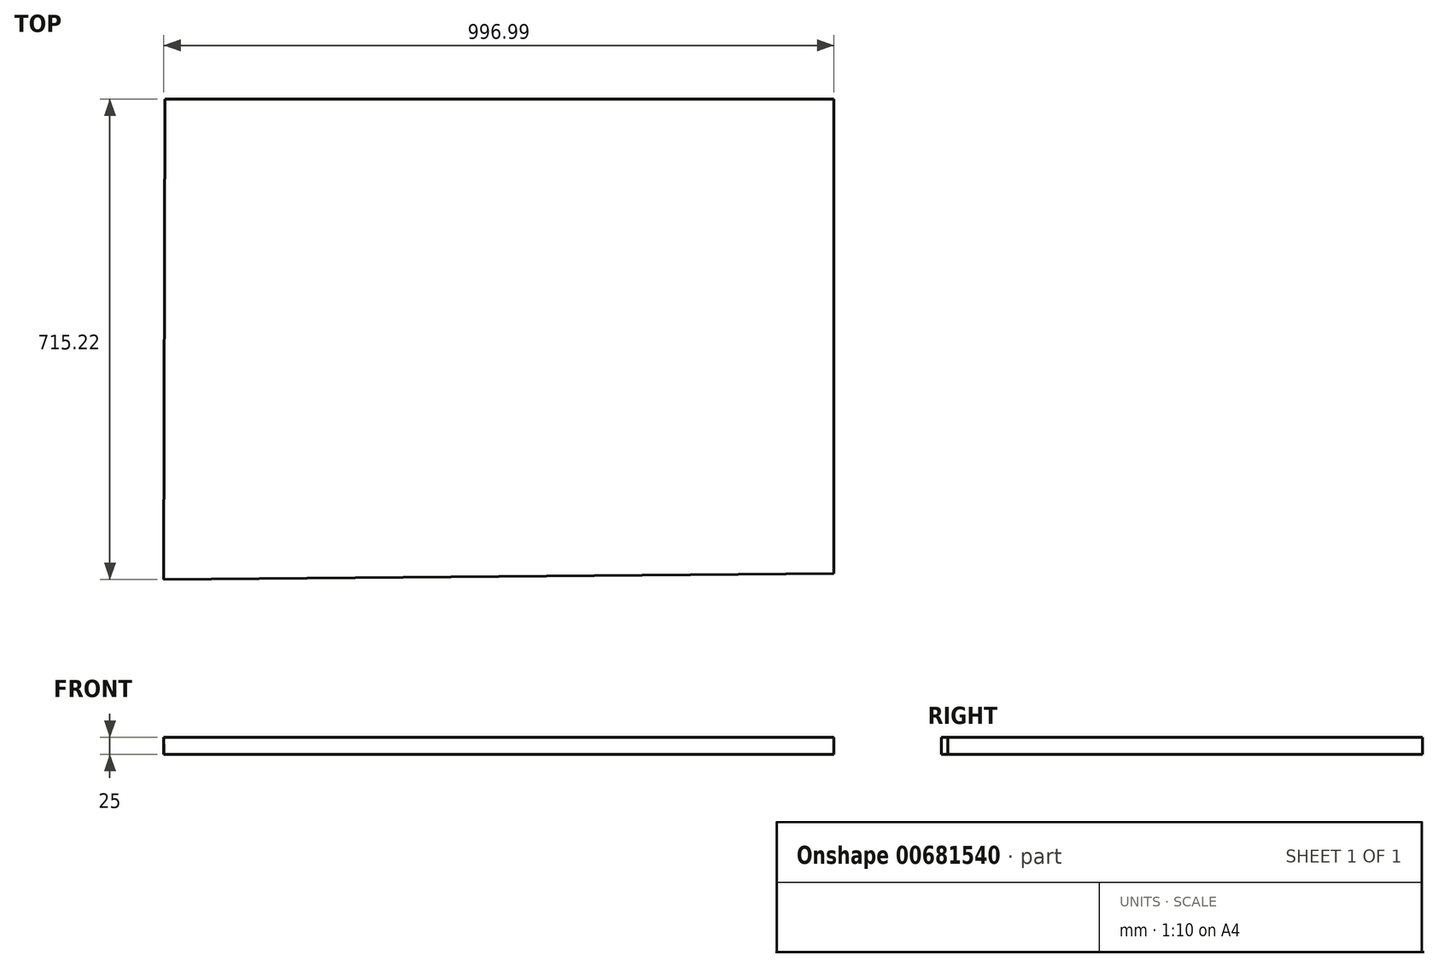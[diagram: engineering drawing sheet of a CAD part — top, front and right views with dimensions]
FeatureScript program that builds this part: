
annotation { "Feature Type Name" : "Feature", "Feature Type Description" : "" }
export const myFeature = defineFeature(function(context is Context, id is Id, definition is map)
    precondition{}
    {
        {
            var Q0;
            Q0=qCreatedBy(makeId("Top.planeOp"),FACE);
            var sketch = newSketch(context, id + "F0", { "sketchPlane" : qUnion([Q0])});
            skLineSegment(sketch, "E0", {"start": v(0, 0) * mm, "end": v(995, 0) * mm});
            skCircle(sketch, "E1", {"center": v(0, 0) * mm, "radius": 1220 * mm});
            skCircle(sketch, "E2", {"center": v(995, 0) * mm, "radius": 1227 * mm});
            skCircle(sketch, "E3", {"center": v(995, 0) * mm, "radius": 706 * mm});
            skCircle(sketch, "E4", {"center": v(994.97, -706) * mm, "radius": 997 * mm});
            skLineSegment(sketch, "E5", {"start": v(994.97, -706) * mm, "end": v(-1.99, -715.22) * mm});
            skLineSegment(sketch, "E6", {"start": v(995, 0) * mm, "end": v(994.97, -706) * mm});
            skLineSegment(sketch, "E7", {"start": v(-1.99, -715.22) * mm, "end": v(0, 0) * mm});
            skSolve(sketch);
        }
        {
            var Q0;
            Q0=sQuery(id+"F0.wireOp",EDGE,"E0");
            var Q1;
            Q1=sQuery(id+"F0.wireOp",EDGE,"E6");
            var Q2;
            Q2=sQuery(id+"F0.wireOp",EDGE,"E5");
            var Q3;
            Q3=sQuery(id+"F0.wireOp",EDGE,"E7");
            extrude(context, id + "F1", {"bodyType" : ToolBodyType.SURFACE, "surfaceEntities" : qUnion([Q0, Q1, Q2, Q3]), "depth" : 25 * mm, "offsetDistance" : 25 * mm});
        }
    });
